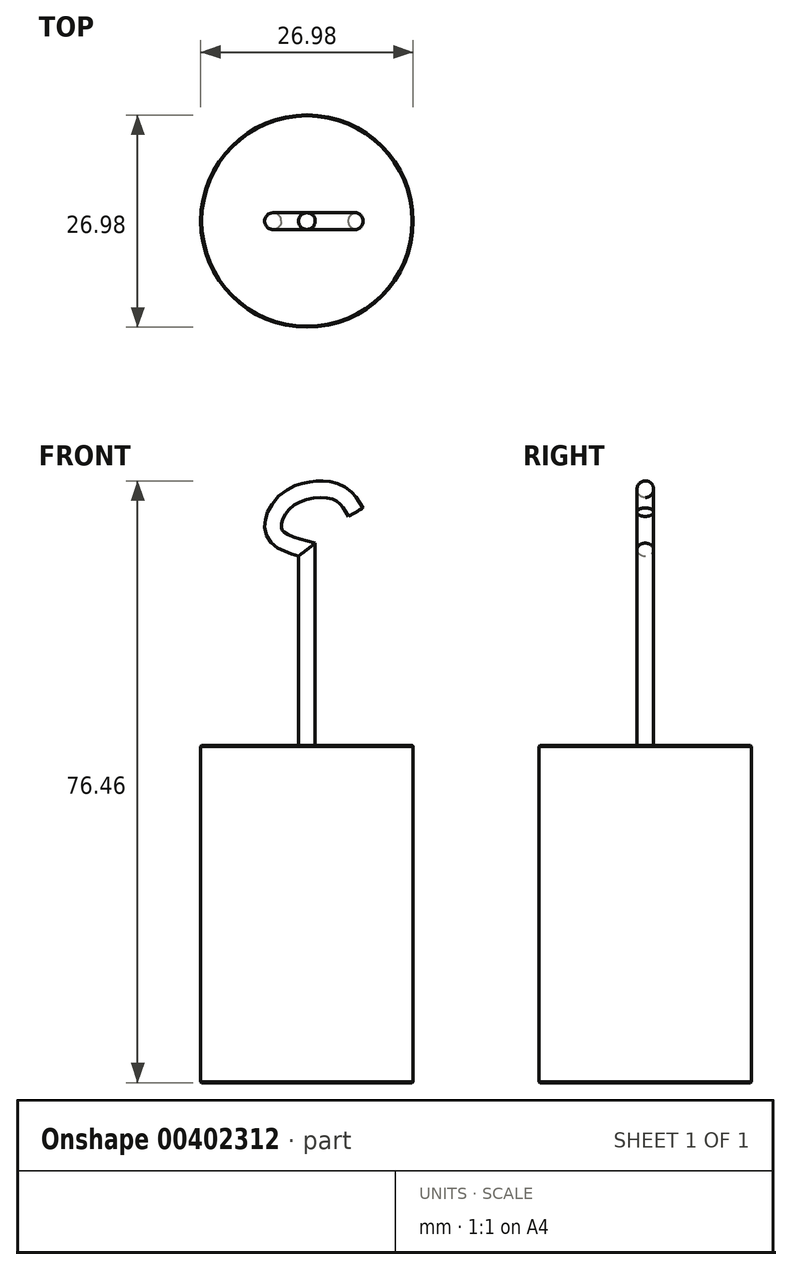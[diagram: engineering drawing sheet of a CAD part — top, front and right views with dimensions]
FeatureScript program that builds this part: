
annotation { "Feature Type Name" : "Feature", "Feature Type Description" : "" }
export const myFeature = defineFeature(function(context is Context, id is Id, definition is map)
    precondition{}
    {
        {
            var Q0;
            Q0=qCreatedBy(makeId("Top.planeOp"),FACE);
            var sketch = newSketch(context, id + "F0", { "sketchPlane" : qUnion([Q0])});
            skCircle(sketch, "E0", {"center": v(0, 0) * mm, "radius": 13.5 * mm});
            skSolve(sketch);
        }
        {
            var Q0;
            Q0 = qSketchRegion(id + "F0", true);
            extrude(context, id + "F1", {"entities" : qUnion([Q0]), "depth" : 42.86 * mm, "symmetric" : true});
        }
        {
            var Q0;
            Q0=qCreatedBy(makeId("Front.planeOp"),FACE);
            var sketch = newSketch(context, id + "F2", { "sketchPlane" : qUnion([Q0])});
            skLineSegment(sketch, "E1", {"start": v(0, 21.43) * mm, "end": v(0, 46.3) * mm});
            skPoint(sketch, "E1.endSnap0", {"position": v(0, 21.43) * mm});
            skFitSpline(sketch, "E2", {"points": [v(0, 46.3) * mm, v(-4.16, 48.45) * mm, v(-2.43, 52.66) * mm, v(3.72, 53.63) * mm, v(6.2, 51.04) * mm], "startDerivative": vector(-21.9, 5.76) * mm, "endDerivative": vector(8.46, -14.4) * mm});
            skPoint(sketch, "E3.orphan", {"position": v(-13.5, 21.43) * mm});
            skPoint(sketch, "E4.0.end.orphan", {"position": v(13.5, 21.43) * mm});
            skSolve(sketch);
        }
        {
            var Q0;
            Q0=makeQuery(id+"F1.opExtrude","CAP_FACE",FACE,{"disambiguationData":[OSD([sQuery(id+"F0.wireOp",EDGE,"E0")])],"isStart":false});
            var sketch = newSketch(context, id + "F3", { "sketchPlane" : qUnion([Q0])});
            skCircle(sketch, "E5", {"center": v(0, 0) * mm, "radius": 1.06 * mm});
            skSolve(sketch);
        }
        {
            var Q0;
            Q0 = qSketchRegion(id + "F3", true);
            var Q1;
            Q1 = qConstructionFilter(qBodyType(qCreatedBy(id + "F2" ,EDGE), BodyType.WIRE), ConstructionObject.NO);
            sweep(context, id + "F4", {"operationType" : NewBodyOperationType.ADD, "profiles" : qUnion([Q0]), "path" : qUnion([Q1])});
        }
        {
            var Q0;
            Q0=makeQuery(id+"F1.opExtrude","CAP_EDGE",EDGE,{"disambiguationData":[OSD([sQuery(id+"F0.wireOp",EDGE,"E0")])],"isStart":false});
            var Q1;
            Q1=makeQuery(id+"F1.opExtrude","CAP_EDGE",EDGE,{"disambiguationData":[OSD([sQuery(id+"F0.wireOp",EDGE,"E0")])],"isStart":true});
            chamfer(context, id + "F5", {"entities" : qUnion([Q0, Q1]), "width" : 0.13 * mm, "tangentPropagation" : true});
        }
    });
